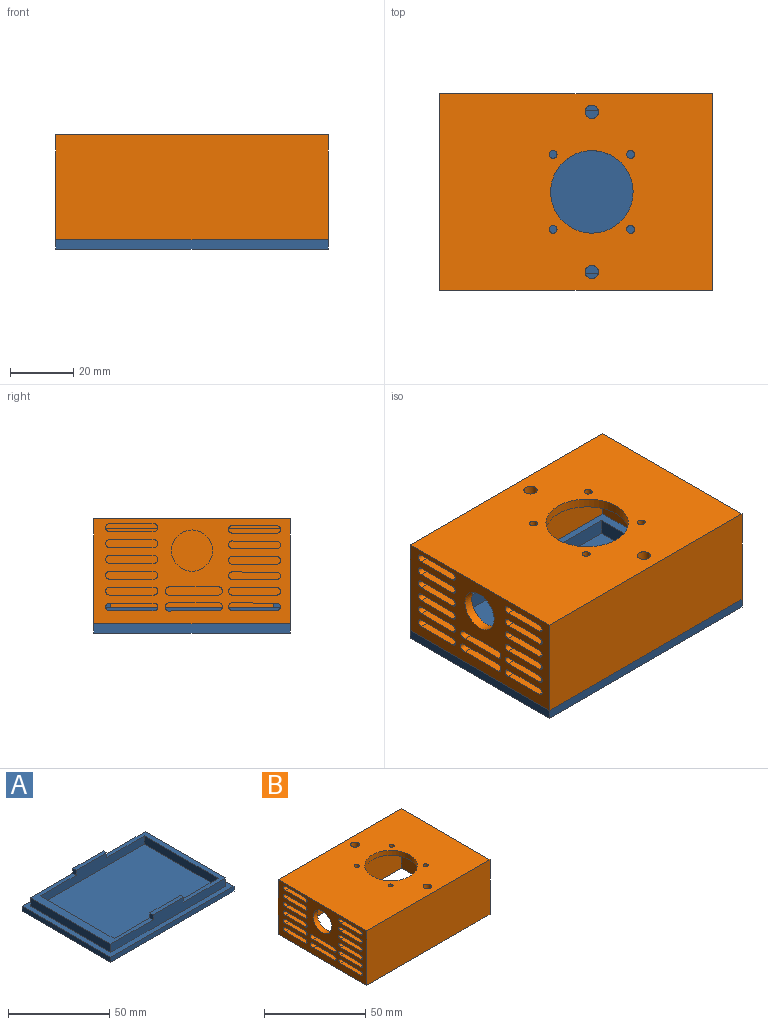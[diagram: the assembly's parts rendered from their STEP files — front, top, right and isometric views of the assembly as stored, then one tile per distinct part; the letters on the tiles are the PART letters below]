
ASSEMBLY  parts=2 mates=1
PART A: 23 faces, bbox 86x62x11 mm
  f0: plane 72.73x51.5mm, normal (0,0,1), area 3745.7mm2, adj f2,f3,f7,f9
  f1: plane 86x62mm, normal (0,0,1), area 852mm2, adj f4,f5,f6,f10,f12,f13,f14,f15
  f2: plane 51.5x5mm, normal (1,0,0), area 257.5mm2, adj f0,f3,f7,f8
  f3: plane 72.73x8mm, normal (0,-1,0), area 427.1mm2, adj f0,f2,f8,f9,f11,f17,f18,f19
  f4: plane 80x8mm, normal (0,1,0), area 463.5mm2, adj f1,f5,f8,f10,f11,f17,f18,f19
  f5: plane 56x5mm, normal (-1,0,0), area 280mm2, adj f1,f4,f6,f8
  f6: plane 80x8mm, normal (0,-1,0), area 463.5mm2, adj f1,f5,f8,f10,f11,f20,f21,f22
  f7: plane 72.73x8mm, normal (0,1,0), area 427.1mm2, adj f0,f2,f8,f9,f11,f20,f21,f22
  f8: plane 56x29.55mm, normal (0,0,1), area 364.7mm2, adj f2,f3,f4,f5,f6,f7,f17,f20
  f9: plane 51.5x5mm, normal (-1,0,0), area 257.5mm2, adj f0,f3,f7,f11
  f10: plane 56x5mm, normal (1,0,0), area 280mm2, adj f1,f4,f6,f11
  f11: plane 56x29.29mm, normal (0,0,1), area 274.3mm2, adj f3,f4,f6,f7,f9,f10,f18,f21
  f12: plane 86x3mm, normal (0,-1,0), area 258mm2, adj f1,f13,f15,f16
  f13: plane 62x3mm, normal (1,0,0), area 186mm2, adj f1,f12,f14,f16
  f14: plane 86x3mm, normal (0,1,0), area 258mm2, adj f1,f13,f15,f16
  f15: plane 62x3mm, normal (-1,0,0), area 186mm2, adj f1,f12,f14,f16
  f16: plane 86x62mm, normal (0,0,-1), area 5332mm2, adj f12,f13,f14,f15
  f17: plane 3x2.25mm, normal (-1,0,0), area 6.7mm2, adj f3,f4,f8,f19
  f18: plane 3x2.25mm, normal (1,0,0), area 6.7mm2, adj f3,f4,f11,f19
  f19: plane 21.16x2.25mm, normal (0,0,1), area 47.6mm2, adj f3,f4,f17,f18
  f20: plane 3x2.25mm, normal (-1,0,0), area 6.7mm2, adj f6,f7,f8,f22
  f21: plane 3x2.25mm, normal (1,0,0), area 6.7mm2, adj f6,f7,f11,f22
  f22: plane 21.16x2.25mm, normal (0,0,1), area 47.6mm2, adj f6,f7,f20,f21
PART B: 77 faces, bbox 86x62x33 mm
  f0: plane 62x33mm, normal (-1,0,0), area 1355.3mm2, adj f3,f4,f7,f11,f16,f17,f18,f19
  f1: plane 56x30mm, normal (1,0,0), area 1026.7mm2, adj f2,f8,f10,f11,f16,f17,f18,f19
  f2: plane 80x56mm, normal (0,0,-1), area 3901.7mm2, adj f1,f5,f8,f9,f10,f12,f13,f14
  f3: plane 86x33mm, normal (0,1,0), area 2838mm2, adj f0,f6,f7,f11
  f4: plane 86x33mm, normal (0,-1,0), area 2838mm2, adj f0,f6,f7,f11
  f5: cylinder r=13mm len=26mm, axis (0,0,-1), area 245mm2, adj f2,f7
  f6: plane 62x33mm, normal (1,0,0), area 2046mm2, adj f3,f4,f7,f11
  f7: plane 86x62mm, normal (0,0,1), area 4753.7mm2, adj f0,f3,f4,f5,f6,f12,f13,f14
  f8: plane 80x30mm, normal (0,-1,0), area 2400mm2, adj f1,f2,f9,f11
  f9: plane 56x30mm, normal (-1,0,0), area 1680mm2, adj f2,f8,f10,f11
  f10: plane 80x30mm, normal (0,1,0), area 2400mm2, adj f1,f2,f9,f11
  f11: plane 86x62mm, normal (0,0,-1), area 852mm2, adj f0,f1,f3,f4,f6,f8,f9,f10
  f12: cylinder r=1.25mm len=3mm, axis (0,0,-1), area 23.6mm2, adj f2,f7
  f13: cylinder r=1.25mm len=3mm, axis (0,0,-1), area 23.6mm2, adj f2,f7
  f14: cylinder r=1.25mm len=3mm, axis (0,0,-1), area 23.6mm2, adj f2,f7
  f15: cylinder r=1.25mm len=3mm, axis (0,0,-1), area 23.6mm2, adj f2,f7
  f16: cylinder r=6.5mm len=13mm, axis (-1,0,0), area 122.5mm2, adj f0,f1
  f17: plane 15x3mm, normal (0,0,-1), area 45mm2, adj f0,f1,f18,f20
  f18: cylinder r=1.36mm len=3mm, axis (-1,0,0), area 14.4mm2, adj f0,f1,f17,f19
  f19: plane 15x3mm, normal (0,0,1), area 45mm2, adj f0,f1,f18,f20
  f20: cylinder r=1.33mm len=3mm, axis (-1,0,0), area 12.5mm2, adj f0,f1,f17,f19
  f21: plane 16.5x1.48mm, normal (-1,0,0), area 23.7mm2, adj f2,f22,f23,f25
  f22: plane 14x3mm, normal (0,0,-1), area 42mm2, adj f0,f21,f23,f25
  f23: cylinder r=1.25mm len=3mm, axis (-1,0,0), area 11.8mm2, adj f0,f1,f21,f22,f24
  f24: plane 14x3mm, normal (0,0,1), area 42mm2, adj f0,f1,f23,f25
  f25: cylinder r=1.25mm len=3mm, axis (-1,0,0), area 11.8mm2, adj f0,f1,f21,f22,f24
  f26: plane 14x3mm, normal (0,0,-1), area 42mm2, adj f0,f1,f27,f29
  f27: cylinder r=1.25mm len=3mm, axis (-1,0,0), area 11.8mm2, adj f0,f1,f26,f28
  f28: plane 14x3mm, normal (0,0,1), area 42mm2, adj f0,f1,f27,f29
  f29: cylinder r=1.25mm len=3mm, axis (-1,0,0), area 11.8mm2, adj f0,f1,f26,f28
  f30: plane 14x3mm, normal (0,0,-1), area 42mm2, adj f0,f1,f31,f33
  f31: cylinder r=1.25mm len=3mm, axis (-1,0,0), area 11.8mm2, adj f0,f1,f30,f32
  f32: plane 14x3mm, normal (0,0,1), area 42mm2, adj f0,f1,f31,f33
  f33: cylinder r=1.25mm len=3mm, axis (-1,0,0), area 11.8mm2, adj f0,f1,f30,f32
  f34: plane 14x3mm, normal (0,0,-1), area 42mm2, adj f0,f1,f35,f37
  f35: cylinder r=1.25mm len=3mm, axis (-1,0,0), area 11.8mm2, adj f0,f1,f34,f36
  f36: plane 14x3mm, normal (0,0,1), area 42mm2, adj f0,f1,f35,f37
  f37: cylinder r=1.25mm len=3mm, axis (-1,0,0), area 11.8mm2, adj f0,f1,f34,f36
  f38: plane 14x3mm, normal (0,0,-1), area 42mm2, adj f0,f1,f39,f41
  f39: cylinder r=1.25mm len=3mm, axis (-1,0,0), area 11.8mm2, adj f0,f1,f38,f40
  f40: plane 14x3mm, normal (0,0,1), area 42mm2, adj f0,f1,f39,f41
  f41: cylinder r=1.25mm len=3mm, axis (-1,0,0), area 11.8mm2, adj f0,f1,f38,f40
  f42: plane 15x3mm, normal (0,0,1), area 45mm2, adj f0,f1,f43,f44
  f43: cylinder r=1.36mm len=3mm, axis (-1,0,0), area 14.4mm2, adj f0,f1,f42,f45
  f44: cylinder r=1.33mm len=3mm, axis (-1,0,0), area 12.5mm2, adj f0,f1,f42,f45
  f45: plane 15x3mm, normal (0,0,-1), area 45mm2, adj f0,f1,f43,f44
  f46: plane 13.99x3mm, normal (0,0,1), area 42mm2, adj f0,f1,f47,f48
  f47: cylinder r=1.23mm len=3mm, axis (-1,0,0), area 12.4mm2, adj f0,f1,f46,f49
  f48: cylinder r=1.17mm len=3mm, axis (-1,0,0), area 11.1mm2, adj f0,f1,f46,f49
  f49: plane 13.74x3mm, normal (0,0.01,-1), area 41.2mm2, adj f0,f1,f47,f48
  f50: plane 13.99x3mm, normal (0,0,1), area 42mm2, adj f0,f1,f51,f53
  f51: cylinder r=1.17mm len=3mm, axis (-1,0,0), area 11.1mm2, adj f0,f1,f50,f52
  f52: plane 13.74x3mm, normal (0,0.01,-1), area 41.2mm2, adj f0,f1,f51,f53
  f53: cylinder r=1.23mm len=3mm, axis (-1,0,0), area 12.4mm2, adj f0,f1,f50,f52
  f54: plane 13.99x3mm, normal (0,0,1), area 42mm2, adj f0,f1,f55,f57
  f55: cylinder r=1.17mm len=3mm, axis (-1,0,0), area 11.1mm2, adj f0,f1,f54,f56
  f56: plane 13.74x3mm, normal (0,0.01,-1), area 41.2mm2, adj f0,f1,f55,f57
  f57: cylinder r=1.23mm len=3mm, axis (-1,0,0), area 12.4mm2, adj f0,f1,f54,f56
  f58: plane 14x3mm, normal (0,0,-1), area 42mm2, adj f0,f1,f59,f61
  f59: cylinder r=1.25mm len=3mm, axis (-1,0,0), area 11.8mm2, adj f0,f1,f58,f60
  f60: plane 14x3mm, normal (0,0,1), area 42mm2, adj f0,f1,f59,f61
  f61: cylinder r=1.25mm len=3mm, axis (-1,0,0), area 11.8mm2, adj f0,f1,f58,f60
  f62: plane 16.31x0.93mm, normal (-1,0,0), area 13.7mm2, adj f2,f64,f65,f66
  f63: plane 13.99x3mm, normal (0,0,1), area 42mm2, adj f0,f1,f64,f66
  f64: cylinder r=1.17mm len=3mm, axis (-1,0,0), area 11.1mm2, adj f0,f1,f62,f63,f65
  f65: plane 13.74x3mm, normal (0,0.01,-1), area 41.2mm2, adj f0,f62,f64,f66
  f66: cylinder r=1.23mm len=3mm, axis (-1,0,0), area 12.4mm2, adj f0,f1,f62,f63,f65
  f67: plane 13.99x3mm, normal (0,0,1), area 42mm2, adj f0,f1,f68,f70
  f68: cylinder r=1.17mm len=3mm, axis (-1,0,0), area 11.1mm2, adj f0,f1,f67,f69
  f69: plane 13.74x3mm, normal (0,0.01,-1), area 41.2mm2, adj f0,f1,f68,f70
  f70: cylinder r=1.23mm len=3mm, axis (-1,0,0), area 12.4mm2, adj f0,f1,f67,f69
  f71: plane 13.99x3mm, normal (0,0,1), area 42mm2, adj f0,f1,f72,f74
  f72: cylinder r=1.17mm len=3mm, axis (-1,0,0), area 11.1mm2, adj f0,f1,f71,f73
  f73: plane 13.74x3mm, normal (0,0.01,-1), area 41.2mm2, adj f0,f1,f72,f74
  f74: cylinder r=1.23mm len=3mm, axis (-1,0,0), area 12.4mm2, adj f0,f1,f71,f73
  f75: cylinder r=2.1mm len=4.2mm, axis (0,0,-1), area 39.6mm2, adj f2,f7
  f76: cylinder r=2.1mm len=4.2mm, axis (0,0,-1), area 39.6mm2, adj f2,f7
PLACE A t=(-0.07,-0.88,46.24)mm fixed
PLACE B t=(-0.07,-0.88,26.24)mm
MATE fastened A.f1 <-> B.f11  axis (0,0,1) through (42.93,-31.88,-3.76)mm
